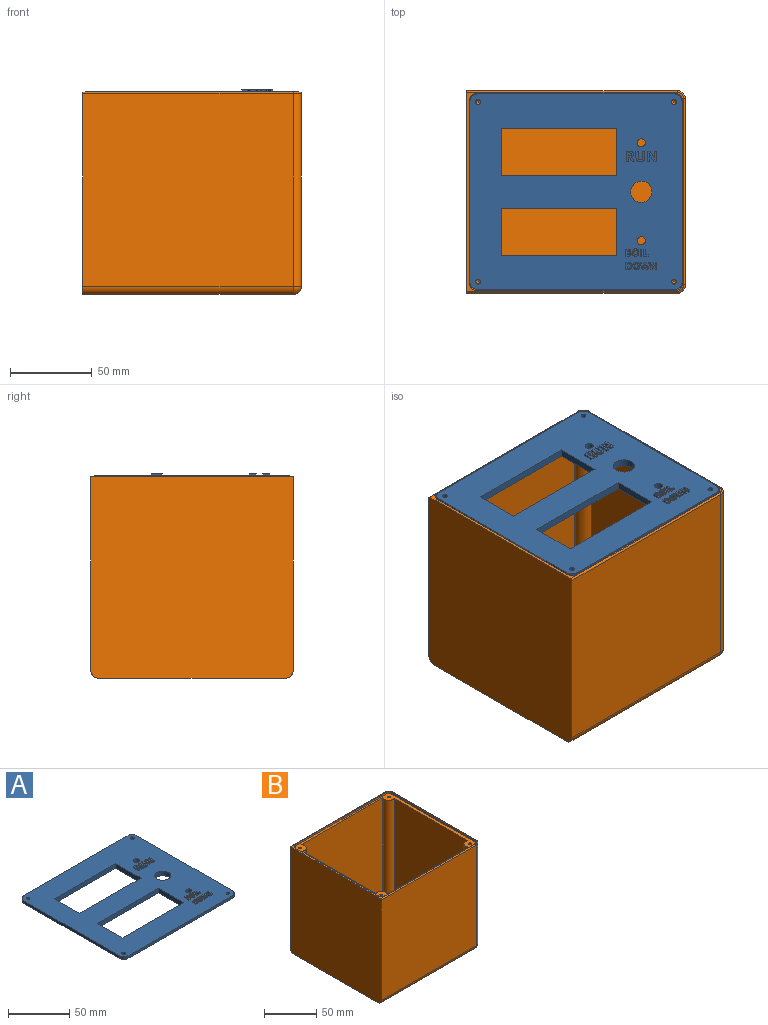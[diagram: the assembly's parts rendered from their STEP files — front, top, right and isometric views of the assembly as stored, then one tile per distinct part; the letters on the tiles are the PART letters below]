
ASSEMBLY  parts=2 mates=1
PART A: 233 faces, bbox 130x120x5.6 mm
  f0: plane 106x96mm, normal (0,0,-1), area 5005.3mm2, adj f207,f208,f209,f210,f213,f214,f215,f216
  f1: plane 130x120mm, normal (0,0,-1), area 4550.3mm2, adj f9,f10,f11,f13,f196,f197,f198,f199
  f2: plane 130x120mm, normal (0,0,1), area 11133.1mm2, adj f3,f4,f5,f6,f7,f8,f9,f10
  f3: plane 70.5x4.6mm, normal (0,1,0), area 324.3mm2, adj f2,f4,f17,f217
  f4: plane 29x4.6mm, normal (1,0,0), area 133.4mm2, adj f2,f3,f5,f217
  f5: plane 70.5x4.6mm, normal (0,-1,0), area 324.3mm2, adj f2,f4,f17,f217
  f6: plane 70.5x4.6mm, normal (0,1,0), area 324.3mm2, adj f2,f7,f12,f222
  f7: plane 29x4.6mm, normal (1,0,0), area 133.4mm2, adj f2,f6,f8,f222
  f8: plane 70.5x4.6mm, normal (0,-1,0), area 324.3mm2, adj f2,f7,f12,f222
  f9: plane 110x2.6mm, normal (-1,0,0), area 286mm2, adj f1,f2,f196,f199
  f10: plane 120x2.6mm, normal (0,-1,0), area 312mm2, adj f1,f2,f196,f197
  f11: plane 110x2.6mm, normal (1,0,0), area 286mm2, adj f1,f2,f197,f198
  f12: plane 29x4.6mm, normal (-1,0,0), area 133.4mm2, adj f2,f6,f8,f222
  f13: plane 120x2.6mm, normal (0,1,0), area 312mm2, adj f1,f2,f198,f199
  f14: cylinder r=2.5mm len=5mm, axis (0,0,1), area 72.3mm2, adj f2,f224
  f15: cylinder r=2.5mm len=5mm, axis (0,0,1), area 72.3mm2, adj f2,f228
  f16: cylinder r=6.5mm len=13mm, axis (0,0,1), area 187.9mm2, adj f2,f226
  f17: plane 29x4.6mm, normal (-1,0,0), area 133.4mm2, adj f2,f3,f5,f217
  f18: plane 1.75x1mm, normal (1,0,0), area 1.7mm2, adj f19,f36,f37,f38
  f19: plane 1x0.42mm, normal (0,-1,0), area 0.4mm2, adj f18,f20,f37,f38
  f20: extruded ~1x0.98mm, area 1mm2, adj f19,f21,f37,f38
  f21: extruded ~1x0.66mm, area 0.8mm2, adj f20,f22,f37,f38
  f22: extruded ~1x0.68mm, area 0.8mm2, adj f21,f23,f37,f38
  f23: extruded ~1x0.96mm, area 1mm2, adj f22,f36,f37,f38
  f24: plane 1x0.73mm, normal (0,-1,0), area 0.7mm2, adj f2,f25,f35,f37
  f25: plane 2.49x1.55mm, normal (-0.85,-0.53,0), area 2.9mm2, adj f2,f24,f26,f37
  f26: plane 1.52x1mm, normal (0,-1,0), area 1.5mm2, adj f2,f25,f27,f37
  f27: extruded ~2.82x1.91mm, area 3.4mm2, adj f2,f26,f28,f37
  f28: extruded ~1x0.89mm, area 1.1mm2, adj f2,f27,f29,f37
  f29: extruded ~1.02x1mm, area 1.1mm2, adj f2,f28,f30,f37
  f30: extruded ~1.46x1mm, area 1.7mm2, adj f2,f29,f31,f37
  f31: extruded ~1.95x1mm, area 2mm2, adj f2,f30,f32,f37
  f32: plane 1.89x1mm, normal (0,1,0), area 1.9mm2, adj f2,f31,f33,f37
  f33: plane 6.48x1mm, normal (-1,0,0), area 6.5mm2, adj f2,f32,f34,f37
  f34: plane 1.37x1mm, normal (0,-1,0), area 1.4mm2, adj f2,f33,f35,f37
  f35: plane 2.49x1mm, normal (1,0,0), area 2.5mm2, adj f2,f24,f34,f37
  f36: plane 1x0.44mm, normal (0,1,0), area 0.4mm2, adj f18,f23,f37,f38
  f37: plane 6.48x5.18mm, normal (0,0,1), area 20.5mm2, adj f18,f19,f20,f21,f22,f23,f24,f25
  f38: plane 1.75x1.71mm, normal (0,0,1), area 2.6mm2, adj f18,f19,f20,f21,f22,f23,f36
  f39: plane 1.37x1mm, normal (0,1,0), area 1.4mm2, adj f2,f40,f53,f54
  f40: plane 3.96x1mm, normal (-1,0,0), area 4mm2, adj f2,f39,f41,f54
  f41: extruded ~1.11x1mm, area 1.2mm2, adj f2,f40,f42,f54
  f42: extruded ~1x0.98mm, area 1.1mm2, adj f2,f41,f43,f54
  f43: extruded ~1x1mm, area 1.1mm2, adj f2,f42,f44,f54
  f44: extruded ~1.1x1mm, area 1.2mm2, adj f2,f43,f45,f54
  f45: plane 3.97x1mm, normal (1,0,0), area 4mm2, adj f2,f44,f46,f54
  f46: plane 1.37x1mm, normal (0,1,0), area 1.4mm2, adj f2,f45,f47,f54
  f47: plane 4.17x1mm, normal (-1,0,0), area 4.2mm2, adj f2,f46,f48,f54
  f48: extruded ~1.75x1mm, area 1.9mm2, adj f2,f47,f49,f54
  f49: extruded ~1.94x1mm, area 2.1mm2, adj f2,f48,f50,f54
  f50: extruded ~1.44x1mm, area 1.5mm2, adj f2,f49,f51,f54
  f51: extruded ~1x0.93mm, area 1.3mm2, adj f2,f50,f52,f54
  f52: extruded ~1.26x1mm, area 1.3mm2, adj f2,f51,f53,f54
  f53: plane 4.19x1mm, normal (1,0,0), area 4.2mm2, adj f2,f39,f52,f54
  f54: plane 6.57x5.32mm, normal (0,0,1), area 19.2mm2, adj f39,f40,f41,f42,f43,f44,f45,f46
  f55: plane 6.48x1mm, normal (1,0,0), area 6.5mm2, adj f2,f56,f68,f69
  f56: plane 1.24x1mm, normal (0,1,0), area 1.2mm2, adj f2,f55,f57,f69
  f57: plane 3.07x1mm, normal (-1,0,0), area 3.1mm2, adj f2,f56,f58,f69
  f58: extruded ~1.79x1mm, area 1.8mm2, adj f2,f57,f59,f69
  f59: plane 1x0.03mm, normal (0,1,0), area 0mm2, adj f2,f58,f60,f69
  f60: plane 4.85x2.81mm, normal (0.87,0.5,0), area 5.6mm2, adj f2,f59,f61,f69
  f61: plane 1.73x1mm, normal (0,1,0), area 1.7mm2, adj f2,f60,f62,f69
  f62: plane 6.48x1mm, normal (-1,0,0), area 6.5mm2, adj f2,f61,f63,f69
  f63: plane 1.23x1mm, normal (0,-1,0), area 1.2mm2, adj f2,f62,f64,f69
  f64: plane 3.05x1mm, normal (1,0,0), area 3mm2, adj f2,f63,f65,f69
  f65: extruded ~1.85x1mm, area 1.9mm2, adj f2,f64,f66,f69
  f66: plane 1x0.04mm, normal (0,-1,0), area 0mm2, adj f2,f65,f67,f69
  f67: plane 4.9x2.82mm, normal (-0.87,-0.5,0), area 5.7mm2, adj f2,f66,f68,f69
  f68: plane 1.75x1mm, normal (0,-1,0), area 1.7mm2, adj f2,f55,f67,f69
  f69: plane 6.48x5.75mm, normal (0,0,1), area 23.8mm2, adj f55,f56,f57,f58,f59,f60,f61,f62
  f70: plane 4.34x1mm, normal (-1,0,0), area 4.3mm2, adj f2,f71,f94,f95
  f71: plane 1.62x1mm, normal (0,-1,0), area 1.6mm2, adj f2,f70,f72,f95
  f72: extruded ~1.17x1mm, area 1.2mm2, adj f2,f71,f73,f95
  f73: extruded ~1x0.93mm, area 1.1mm2, adj f2,f72,f74,f95
  f74: extruded ~1x0.67mm, area 0.7mm2, adj f2,f73,f75,f95
  f75: extruded ~1x0.6mm, area 0.7mm2, adj f2,f74,f76,f95
  f76: plane 1x0.03mm, normal (1,0,0), area 0mm2, adj f2,f75,f77,f95
  f77: extruded ~1x0.49mm, area 0.6mm2, adj f2,f76,f78,f95
  f78: extruded ~1x0.64mm, area 0.7mm2, adj f2,f77,f79,f95
  f79: extruded ~1x0.84mm, area 1mm2, adj f2,f78,f80,f95
  f80: extruded ~1.34x1mm, area 1.4mm2, adj f2,f79,f94,f95
  f81: plane 1x0.96mm, normal (1,0,0), area 1mm2, adj f82,f92,f95,f97
  f82: plane 1x0.48mm, normal (0,-1,0), area 0.5mm2, adj f81,f83,f95,f97
  f83: extruded ~1x0.58mm, area 0.6mm2, adj f82,f84,f95,f97
  f84: extruded ~1x0.36mm, area 0.4mm2, adj f83,f85,f95,f97
  f85: extruded ~1x0.38mm, area 0.4mm2, adj f84,f86,f95,f97
  f86: extruded ~1x0.54mm, area 0.6mm2, adj f85,f92,f95,f97
  f87: plane 1x0.57mm, normal (0,-1,0), area 0.6mm2, adj f88,f93,f95,f96
  f88: extruded ~1x0.77mm, area 1.1mm2, adj f87,f89,f95,f96
  f89: extruded ~1x0.45mm, area 0.5mm2, adj f88,f90,f95,f96
  f90: extruded ~1x0.56mm, area 0.6mm2, adj f89,f91,f95,f96
  f91: plane 1x0.6mm, normal (0,1,0), area 0.6mm2, adj f90,f93,f95,f96
  f92: plane 1x0.53mm, normal (0,1,0), area 0.5mm2, adj f81,f86,f95,f97
  f93: plane 1.13x1mm, normal (1,0,0), area 1.1mm2, adj f87,f91,f95,f96
  f94: plane 1.35x1mm, normal (0,1,0), area 1.4mm2, adj f2,f70,f80,f95
  f95: plane 4.34x3.22mm, normal (0,0,1), area 10.3mm2, adj f70,f71,f72,f73,f74,f75,f76,f77
  f96: plane 1.34x1.13mm, normal (0,0,1), area 1.4mm2, adj f87,f88,f89,f90,f91,f93
  f97: plane 1.24x0.96mm, normal (0,0,1), area 1.1mm2, adj f81,f82,f83,f84,f85,f86,f92
  f98: extruded ~1.66x1mm, area 1.8mm2, adj f2,f99,f111,f112
  f99: extruded ~1.53x1mm, area 1.7mm2, adj f2,f98,f100,f112
  f100: extruded ~1.54x1mm, area 1.7mm2, adj f2,f99,f101,f112
  f101: extruded ~1.65x1mm, area 1.8mm2, adj f2,f100,f102,f112
  f102: extruded ~1.66x1mm, area 1.8mm2, adj f2,f101,f103,f112
  f103: extruded ~1.53x1mm, area 1.7mm2, adj f2,f102,f104,f112
  f104: extruded ~1.53x1mm, area 1.7mm2, adj f2,f103,f111,f112
  f105: extruded ~1.1x1mm, area 1.1mm2, adj f106,f110,f112,f113
  f106: extruded ~1x0.83mm, area 0.9mm2, adj f105,f107,f112,f113
  f107: extruded ~1.47x1.1mm, area 2.1mm2, adj f106,f108,f112,f113
  f108: extruded ~1.46x1.1mm, area 2.1mm2, adj f107,f109,f112,f113
  f109: extruded ~1x0.82mm, area 0.9mm2, adj f108,f110,f112,f113
  f110: extruded ~1.1x1mm, area 1.1mm2, adj f105,f109,f112,f113
  f111: extruded ~1.66x1mm, area 1.8mm2, adj f2,f98,f104,f112
  f112: plane 4.47x4.13mm, normal (0,0,1), area 9.9mm2, adj f98,f99,f100,f101,f102,f103,f104,f105
  f113: plane 2.93x2.2mm, normal (0,0,1), area 5.4mm2, adj f105,f106,f107,f108,f109,f110
  f114: plane 1x0.92mm, normal (0,-1,0), area 0.9mm2, adj f2,f115,f117,f118
  f115: plane 4.34x1mm, normal (1,0,0), area 4.3mm2, adj f2,f114,f116,f118
  f116: plane 1x0.92mm, normal (0,1,0), area 0.9mm2, adj f2,f115,f117,f118
  f117: plane 4.34x1mm, normal (-1,0,0), area 4.3mm2, adj f2,f114,f116,f118
  f118: plane 4.34x0.92mm, normal (0,0,1), area 4mm2, adj f114,f115,f116,f117
  f119: plane 2.68x1mm, normal (0,-1,0), area 2.7mm2, adj f2,f120,f124,f125
  f120: plane 1x0.76mm, normal (1,0,0), area 0.8mm2, adj f2,f119,f121,f125
  f121: plane 1.76x1mm, normal (0,1,0), area 1.8mm2, adj f2,f120,f122,f125
  f122: plane 3.58x1mm, normal (1,0,0), area 3.6mm2, adj f2,f121,f123,f125
  f123: plane 1x0.92mm, normal (0,1,0), area 0.9mm2, adj f2,f122,f124,f125
  f124: plane 4.34x1mm, normal (-1,0,0), area 4.3mm2, adj f2,f119,f123,f125
  f125: plane 4.34x2.68mm, normal (0,0,1), area 5.3mm2, adj f119,f120,f121,f122,f123,f124
  f126: extruded ~1.57x1mm, area 1.7mm2, adj f2,f127,f137,f138
  f127: extruded ~1.65x1mm, area 1.8mm2, adj f2,f126,f128,f138
  f128: plane 1.36x1mm, normal (0,1,0), area 1.4mm2, adj f2,f127,f129,f138
  f129: plane 4.34x1mm, normal (-1,0,0), area 4.3mm2, adj f2,f128,f130,f138
  f130: plane 1.23x1mm, normal (0,-1,0), area 1.2mm2, adj f2,f129,f131,f138
  f131: extruded ~1.76x1mm, area 1.9mm2, adj f2,f130,f137,f138
  f132: extruded ~1.43x1.33mm, area 2.2mm2, adj f133,f136,f138,f139
  f133: plane 1x0.39mm, normal (0,1,0), area 0.4mm2, adj f132,f134,f138,f139
  f134: plane 2.83x1mm, normal (1,0,0), area 2.8mm2, adj f133,f135,f138,f139
  f135: plane 1x0.49mm, normal (0,-1,0), area 0.5mm2, adj f134,f136,f138,f139
  f136: extruded ~1.4x1.23mm, area 2.1mm2, adj f132,f135,f138,f139
  f137: extruded ~1.64x1mm, area 1.8mm2, adj f2,f126,f131,f138
  f138: plane 4.34x3.6mm, normal (0,0,1), area 9.6mm2, adj f126,f127,f128,f129,f130,f131,f132,f133
  f139: plane 2.83x1.72mm, normal (0,0,1), area 4.3mm2, adj f132,f133,f134,f135,f136
  f140: extruded ~1.66x1mm, area 1.8mm2, adj f2,f141,f153,f154
  f141: extruded ~1.53x1mm, area 1.7mm2, adj f2,f140,f142,f154
  f142: extruded ~1.54x1mm, area 1.7mm2, adj f2,f141,f143,f154
  f143: extruded ~1.65x1mm, area 1.8mm2, adj f2,f142,f144,f154
  f144: extruded ~1.66x1mm, area 1.8mm2, adj f2,f143,f145,f154
  f145: extruded ~1.53x1mm, area 1.7mm2, adj f2,f144,f146,f154
  f146: extruded ~1.53x1mm, area 1.7mm2, adj f2,f145,f153,f154
  f147: extruded ~1.1x1mm, area 1.1mm2, adj f148,f152,f154,f155
  f148: extruded ~1x0.83mm, area 0.9mm2, adj f147,f149,f154,f155
  f149: extruded ~1.47x1.1mm, area 2.1mm2, adj f148,f150,f154,f155
  f150: extruded ~1.46x1.1mm, area 2.1mm2, adj f149,f151,f154,f155
  f151: extruded ~1x0.82mm, area 0.9mm2, adj f150,f152,f154,f155
  f152: extruded ~1.1x1mm, area 1.1mm2, adj f147,f151,f154,f155
  f153: extruded ~1.66x1mm, area 1.8mm2, adj f2,f140,f146,f154
  f154: plane 4.47x4.13mm, normal (0,0,1), area 9.9mm2, adj f140,f141,f142,f143,f144,f145,f146,f147
  f155: plane 2.93x2.2mm, normal (0,0,1), area 5.4mm2, adj f147,f148,f149,f150,f151,f152
  f156: plane 4.34x1.1mm, normal (0.97,-0.25,0), area 4.5mm2, adj f2,f157,f179,f180
  f157: plane 1x0.91mm, normal (0,1,0), area 0.9mm2, adj f2,f156,f158,f180
  f158: plane 2.37x1mm, normal (-0.97,0.23,0), area 2.4mm2, adj f2,f157,f159,f180
  f159: extruded ~1x0.56mm, area 0.6mm2, adj f2,f158,f160,f180
  f160: extruded ~1x0.58mm, area 0.6mm2, adj f2,f159,f161,f180
  f161: extruded ~1x0.58mm, area 0.6mm2, adj f2,f160,f162,f180
  f162: extruded ~1x0.5mm, area 0.5mm2, adj f2,f161,f163,f180
  f163: plane 2.43x1mm, normal (0.97,0.25,0), area 2.5mm2, adj f2,f162,f164,f180
  f164: plane 1x0.87mm, normal (0,1,0), area 0.9mm2, adj f2,f163,f165,f180
  f165: plane 2.43x1mm, normal (-0.97,0.25,0), area 2.5mm2, adj f2,f164,f166,f180
  f166: extruded ~1x0.55mm, area 0.6mm2, adj f2,f165,f167,f180
  f167: extruded ~1x0.52mm, area 0.5mm2, adj f2,f166,f168,f180
  f168: extruded ~1.14x1mm, area 1.2mm2, adj f2,f167,f169,f180
  f169: plane 2.37x1mm, normal (0.97,0.23,0), area 2.4mm2, adj f2,f168,f170,f180
  f170: plane 1x0.91mm, normal (0,1,0), area 0.9mm2, adj f2,f169,f171,f180
  f171: plane 4.34x1.11mm, normal (-0.97,-0.25,0), area 4.5mm2, adj f2,f170,f172,f180
  f172: plane 1.04x1mm, normal (0,-1,0), area 1mm2, adj f2,f171,f173,f180
  f173: plane 2.27x1mm, normal (0.97,-0.25,0), area 2.3mm2, adj f2,f172,f174,f180
  f174: extruded ~1x0.51mm, area 0.5mm2, adj f2,f173,f175,f180
  f175: extruded ~1x0.52mm, area 0.5mm2, adj f2,f174,f176,f180
  f176: extruded ~1x0.51mm, area 0.5mm2, adj f2,f175,f177,f180
  f177: extruded ~1x0.5mm, area 0.5mm2, adj f2,f176,f178,f180
  f178: plane 2.28x1mm, normal (-0.97,-0.25,0), area 2.4mm2, adj f2,f177,f179,f180
  f179: plane 1.05x1mm, normal (0,-1,0), area 1mm2, adj f2,f156,f178,f180
  f180: plane 5.88x4.34mm, normal (0,0,1), area 13mm2, adj f156,f157,f158,f159,f160,f161,f162,f163
  f181: plane 4.34x1mm, normal (1,0,0), area 4.3mm2, adj f2,f182,f194,f195
  f182: plane 1x0.83mm, normal (0,1,0), area 0.8mm2, adj f2,f181,f183,f195
  f183: plane 2.05x1mm, normal (-1,0,0), area 2.1mm2, adj f2,f182,f184,f195
  f184: extruded ~1.2x1mm, area 1.2mm2, adj f2,f183,f185,f195
  f185: plane 1x0.02mm, normal (0,1,0), area 0mm2, adj f2,f184,f186,f195
  f186: plane 3.25x1.88mm, normal (0.87,0.5,0), area 3.8mm2, adj f2,f185,f187,f195
  f187: plane 1.16x1mm, normal (0,1,0), area 1.2mm2, adj f2,f186,f188,f195
  f188: plane 4.34x1mm, normal (-1,0,0), area 4.3mm2, adj f2,f187,f189,f195
  f189: plane 1x0.82mm, normal (0,-1,0), area 0.8mm2, adj f2,f188,f190,f195
  f190: plane 2.04x1mm, normal (1,0,0), area 2mm2, adj f2,f189,f191,f195
  f191: extruded ~1.24x1mm, area 1.2mm2, adj f2,f190,f192,f195
  f192: plane 1x0.03mm, normal (0,-1,0), area 0mm2, adj f2,f191,f193,f195
  f193: plane 3.28x1.89mm, normal (-0.87,-0.5,0), area 3.8mm2, adj f2,f192,f194,f195
  f194: plane 1.17x1mm, normal (0,-1,0), area 1.2mm2, adj f2,f181,f193,f195
  f195: plane 4.34x3.85mm, normal (0,0,1), area 10.7mm2, adj f181,f182,f183,f184,f185,f186,f187,f188
  f196: cylinder r=5mm len=5mm, axis (0,0,1), area 20.4mm2, adj f1,f2,f9,f10
  f197: cylinder r=5mm len=5mm, axis (0,0,-1), area 20.4mm2, adj f1,f2,f10,f11
  f198: cylinder r=5mm len=5mm, axis (0,0,1), area 20.4mm2, adj f1,f2,f11,f13
  f199: cylinder r=5mm len=5mm, axis (0,0,-1), area 20.4mm2, adj f1,f2,f9,f13
  f200: cylinder r=1.5mm len=3mm, axis (0,0,1), area 24.5mm2, adj f1,f2
  f201: cylinder r=1.5mm len=3mm, axis (0,0,1), area 24.5mm2, adj f1,f2
  f202: cylinder r=1.5mm len=3mm, axis (0,0,1), area 24.5mm2, adj f1,f2
  f203: cylinder r=1.5mm len=3mm, axis (0,0,1), area 24.5mm2, adj f1,f2
  f204: plane 100x1mm, normal (1,0,0), area 100mm2, adj f1,f205,f211,f230
  f205: plane 110x1mm, normal (0,-1,0), area 110mm2, adj f1,f204,f206,f232
  f206: plane 100x1mm, normal (-1,0,0), area 100mm2, adj f1,f205,f211,f231
  f207: plane 106x2mm, normal (0,1,0), area 212mm2, adj f0,f208,f210,f212
  f208: plane 96x2mm, normal (-1,0,0), area 192mm2, adj f0,f207,f209,f212
  f209: plane 106x2mm, normal (0,-1,0), area 212mm2, adj f0,f208,f210,f212
  f210: plane 96x2mm, normal (1,0,0), area 192mm2, adj f0,f207,f209,f212
  f211: plane 110x1mm, normal (0,1,0), area 110mm2, adj f1,f204,f206,f229
  f212: plane 108x98mm, normal (0,0,-1), area 408mm2, adj f207,f208,f209,f210,f229,f230,f231,f232
  f213: plane 33x2mm, normal (1,0,0), area 66mm2, adj f0,f214,f216,f217
  f214: plane 74.5x2mm, normal (0,-1,0), area 149mm2, adj f0,f213,f215,f217
  f215: plane 33x2mm, normal (-1,0,0), area 66mm2, adj f0,f214,f216,f217
  f216: plane 74.5x2mm, normal (0,1,0), area 149mm2, adj f0,f213,f215,f217
  f217: plane 74.5x33mm, normal (0,0,-1), area 414mm2, adj f3,f4,f5,f17,f213,f214,f215,f216
  f218: plane 33x2mm, normal (1,0,0), area 66mm2, adj f0,f219,f221,f222
  f219: plane 74.5x2mm, normal (0,-1,0), area 149mm2, adj f0,f218,f220,f222
  f220: plane 33x2mm, normal (-1,0,0), area 66mm2, adj f0,f219,f221,f222
  f221: plane 74.5x2mm, normal (0,1,0), area 149mm2, adj f0,f218,f220,f222
  f222: plane 74.5x33mm, normal (0,0,-1), area 414mm2, adj f6,f7,f8,f12,f218,f219,f220,f221
  f223: cylinder r=3.5mm len=7mm, axis (0,0,1), area 44mm2, adj f0,f224
  f224: plane 7x7mm, normal (0,0,-1), area 18.8mm2, adj f14,f223
  f225: cylinder r=7.5mm len=15mm, axis (0,0,1), area 94.2mm2, adj f0,f226
  f226: plane 15x15mm, normal (0,0,-1), area 44mm2, adj f16,f225
  f227: cylinder r=3.5mm len=7mm, axis (0,0,1), area 44mm2, adj f0,f228
  f228: plane 7x7mm, normal (0,0,-1), area 18.8mm2, adj f15,f227
  f229: plane 110x1mm, normal (0,0.71,-0.71), area 154.1mm2, adj f211,f212,f230,f231
  f230: plane 100x1mm, normal (0.71,0,-0.71), area 140mm2, adj f204,f212,f229,f232
  f231: plane 100x1mm, normal (-0.71,0,-0.71), area 140mm2, adj f206,f212,f229,f232
  f232: plane 110x1mm, normal (0,-0.71,-0.71), area 154.1mm2, adj f205,f212,f230,f231
PART B: 44 faces, bbox 134.4x124.8x124 mm
  f0: plane 133x122mm, normal (0,0,1), area 389.6mm2, adj f5,f6,f7,f8,f9,f10,f11,f12
  f1: plane 129x118mm, normal (0,-1,0), area 15222mm2, adj f5,f27,f30,f39
  f2: plane 129x114mm, normal (0,0,-1), area 14706mm2, adj f5,f25,f28,f30
  f3: plane 129x118mm, normal (0,1,0), area 15222mm2, adj f5,f24,f25,f42
  f4: plane 118x114mm, normal (1,0,0), area 13452mm2, adj f24,f27,f28,f41
  f5: plane 124x124mm, normal (-1,0,0), area 15364.8mm2, adj f0,f1,f2,f3,f25,f30,f39,f42
  f6: cylinder r=5mm len=5mm, axis (0,0,1), area 15.7mm2, adj f0,f7,f13,f14
  f7: plane 111x2mm, normal (1,0,0), area 222mm2, adj f0,f6,f8,f14
  f8: cylinder r=5mm len=5mm, axis (0,0,1), area 15.7mm2, adj f0,f7,f9,f14
  f9: plane 121x2mm, normal (0,1,0), area 242mm2, adj f0,f8,f10,f14
  f10: cylinder r=5mm len=5mm, axis (0,0,1), area 15.7mm2, adj f0,f9,f11,f14
  f11: plane 111x2mm, normal (-1,0,0), area 222mm2, adj f0,f10,f12,f14
  f12: cylinder r=5mm len=5mm, axis (0,0,1), area 15.7mm2, adj f0,f11,f13,f14
  f13: plane 121x2mm, normal (0,-1,0), area 242mm2, adj f0,f6,f12,f14
  f14: plane 131x121mm, normal (0,0,1), area 1661.3mm2, adj f6,f7,f8,f9,f10,f11,f12,f13
  f15: cylinder r=5.75mm len=118mm, axis (0,0,1), area 1679.2mm2, adj f14,f16,f22,f23
  f16: plane 118x99.22mm, normal (1,0,0), area 11707.7mm2, adj f14,f15,f17,f23
  f17: cylinder r=5.75mm len=118mm, axis (0,0,1), area 1679.2mm2, adj f14,f16,f18,f23
  f18: plane 118x110.19mm, normal (0,1,0), area 13002.3mm2, adj f14,f17,f19,f23
  f19: cylinder r=5.75mm len=118mm, axis (0,0,1), area 1679.2mm2, adj f14,f18,f20,f23
  f20: plane 118x99.22mm, normal (-1,0,0), area 11707.7mm2, adj f14,f19,f21,f23
  f21: cylinder r=5.75mm len=118mm, axis (0,0,1), area 1679.2mm2, adj f14,f20,f22,f23
  f22: plane 118x110.19mm, normal (0,-1,0), area 13002.3mm2, adj f14,f15,f21,f23
  f23: plane 124x116mm, normal (0,0,1), area 14145.3mm2, adj f15,f16,f17,f18,f19,f20,f21,f22
  f24: cylinder r=5mm len=118mm, axis (0,0,-1), area 926.8mm2, adj f3,f4,f26,f43
  f25: cylinder r=5mm len=129mm, axis (-1,0,0), area 1013.2mm2, adj f2,f3,f5,f26
  f26: sphere r=5mm, area 39.3mm2, adj f24,f25,f28
  f27: cylinder r=5mm len=118mm, axis (0,0,1), area 926.8mm2, adj f1,f4,f29,f40
  f28: cylinder r=5mm len=114mm, axis (0,-1,0), area 895.4mm2, adj f2,f4,f26,f29
  f29: sphere r=5mm, area 39.3mm2, adj f27,f28,f30
  f30: cylinder r=5mm len=129mm, axis (1,0,0), area 1013.2mm2, adj f1,f2,f5,f29
  f31: cylinder r=1.35mm len=18mm, axis (0,0,1), area 152.7mm2, adj f14,f32
  f32: cone r=0mm half-angle=59deg, axis (0,0,1), area 6.7mm2, adj f31
  f33: cylinder r=1.35mm len=18mm, axis (0,0,1), area 152.7mm2, adj f14,f34
  f34: cone r=0mm half-angle=59deg, axis (0,0,1), area 6.7mm2, adj f33
  f35: cylinder r=1.35mm len=18mm, axis (0,0,1), area 152.7mm2, adj f14,f36
  f36: cone r=0mm half-angle=59deg, axis (0,0,1), area 6.7mm2, adj f35
  f37: cylinder r=1.35mm len=18mm, axis (0,0,1), area 152.7mm2, adj f14,f38
  f38: cone r=0mm half-angle=59deg, axis (0,0,1), area 6.7mm2, adj f37
  f39: cylinder r=1mm len=129mm, axis (-1,0,0), area 202.6mm2, adj f0,f1,f5,f40
  f40: torus R=4mm, axis (0,0,-1), area 11.4mm2, adj f0,f27,f39,f41
  f41: cylinder r=1mm len=114mm, axis (0,1,0), area 179.1mm2, adj f0,f4,f40,f43
  f42: cylinder r=1mm len=129mm, axis (1,0,0), area 202.6mm2, adj f0,f3,f5,f43
  f43: torus R=4mm, axis (0,0,-1), area 11.4mm2, adj f0,f24,f41,f42
PLACE A t=(83.2,49.24,62.61)mm
PLACE B t=(16.2,14.79,258.27)mm
MATE slider A.f196 <-> B.f17  axis (0,0,-1) through (23.2,-5.76,60.01)mm
